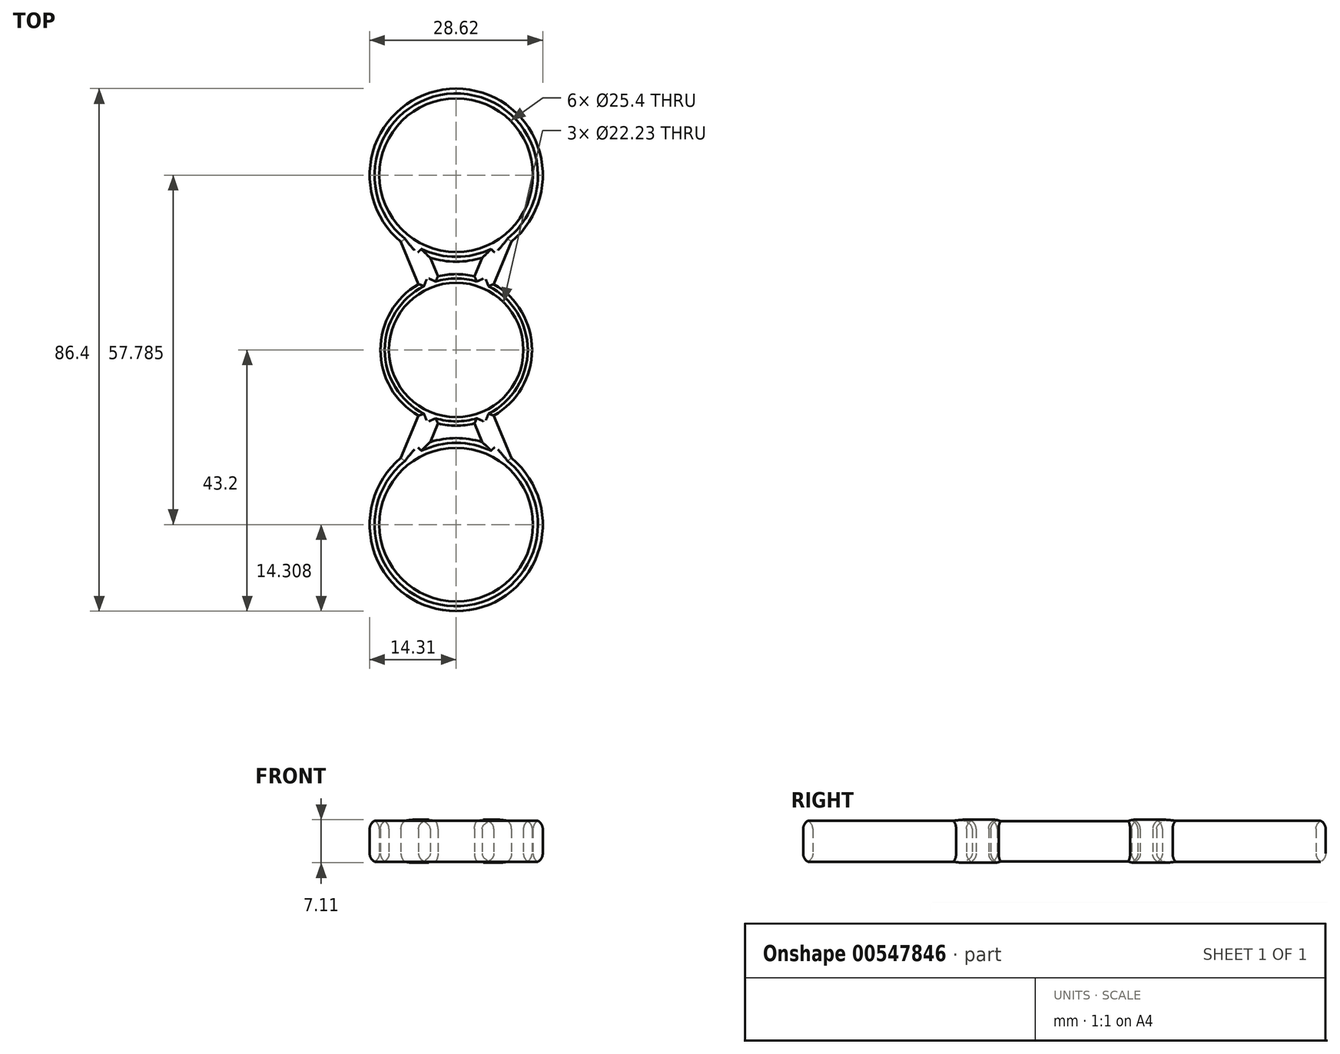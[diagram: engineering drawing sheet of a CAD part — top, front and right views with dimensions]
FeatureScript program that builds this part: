
annotation { "Feature Type Name" : "Feature", "Feature Type Description" : "" }
export const myFeature = defineFeature(function(context is Context, id is Id, definition is map)
    precondition{}
    {
        {
            var Q0;
            Q0=qCreatedBy(makeId("Top.planeOp"),FACE);
            var sketch = newSketch(context, id + "F0", { "sketchPlane" : qUnion([Q0])});
            skCircle(sketch, "E0", {"center": v(0, 0) * mm, "radius": 11.11 * mm});
            skCircle(sketch, "E1", {"center": v(0, 28.9) * mm, "radius": 12.7 * mm});
            skCircle(sketch, "E2", {"center": v(0, -28.9) * mm, "radius": 12.7 * mm});
            skLineSegment(sketch, "E3", {"start": v(-12.07, 24.94) * mm, "end": v(-11.32, 23.13) * mm});
            skLineSegment(sketch, "E4", {"start": v(-4.3, 15.25) * mm, "end": v(-3, 12.16) * mm});
            skLineSegment(sketch, "E5.MirrorCS", {"start": v(4.3, 15.25) * mm, "end": v(3, 12.16) * mm});
            skLineSegment(sketch, "E6.MirrorCS", {"start": v(12.07, 24.94) * mm, "end": v(11.32, 23.13) * mm});
            skLineSegment(sketch, "E7.MirrorCS", {"start": v(-12.07, -24.94) * mm, "end": v(-11.32, -23.13) * mm});
            skLineSegment(sketch, "E8.MirrorCS", {"start": v(-4.3, -15.25) * mm, "end": v(-3, -12.16) * mm});
            skLineSegment(sketch, "E9.MirrorCS", {"start": v(4.3, -15.25) * mm, "end": v(3, -12.16) * mm});
            skLineSegment(sketch, "E10.MirrorCS", {"start": v(12.07, -24.94) * mm, "end": v(11.32, -23.13) * mm});
            skArc(sketch, "E11", {"start": v(-4.3, 15.25) * mm, "mid": v(0, 14.59) * mm, "end": v(4.3, 15.25) * mm});
            skArc(sketch, "E12.MirrorC", {"start": v(-4.3, -15.25) * mm, "mid": v(0, -14.59) * mm, "end": v(4.3, -15.25) * mm});
            skArc(sketch, "E13", {"start": v(-6.23, 10.87) * mm, "mid": v(-12.53, 0) * mm, "end": v(-6.23, -10.87) * mm});
            skPoint(sketch, "E14.orphan", {"position": v(-5.68, 9.55) * mm});
            skPoint(sketch, "E15.orphan", {"position": v(-2.46, 10.84) * mm});
            skArc(sketch, "E16.trimOffspring", {"start": v(3, 12.16) * mm, "mid": v(0, 12.53) * mm, "end": v(-3, 12.16) * mm});
            skPoint(sketch, "E17.orphan", {"position": v(2.46, 10.84) * mm});
            skPoint(sketch, "E18.orphan", {"position": v(5.68, 9.55) * mm});
            skLineSegment(sketch, "E19.trimOffspring", {"start": v(-9.14, 17.89) * mm, "end": v(-6.23, 10.87) * mm});
            skPoint(sketch, "E20.orphan", {"position": v(-5.13, 17.28) * mm});
            skPoint(sketch, "E21.orphan", {"position": v(5.13, 17.28) * mm});
            skLineSegment(sketch, "E22.trimOffspring", {"start": v(9.14, 17.89) * mm, "end": v(6.23, 10.87) * mm});
            skArc(sketch, "E23.trimOffspring", {"start": v(9.14, 17.89) * mm, "mid": v(0, 43.2) * mm, "end": v(-9.14, 17.89) * mm});
            skArc(sketch, "E24.trimOffspring", {"start": v(-3, -12.16) * mm, "mid": v(0, -12.53) * mm, "end": v(3, -12.16) * mm});
            skPoint(sketch, "E25.orphan", {"position": v(-5.68, -9.55) * mm});
            skPoint(sketch, "E26.orphan", {"position": v(-2.46, -10.84) * mm});
            skLineSegment(sketch, "E27.trimOffspring", {"start": v(-9.14, -17.89) * mm, "end": v(-6.23, -10.87) * mm});
            skPoint(sketch, "E28.orphan", {"position": v(-5.13, -17.28) * mm});
            skPoint(sketch, "E29.orphan", {"position": v(2.46, -10.84) * mm});
            skPoint(sketch, "E30.orphan", {"position": v(5.13, -17.28) * mm});
            skArc(sketch, "E31.trimOffspring", {"start": v(9.14, -17.89) * mm, "mid": v(0, -43.2) * mm, "end": v(-9.14, -17.89) * mm});
            skArc(sketch, "E32.trimOffspring", {"start": v(6.23, -10.87) * mm, "mid": v(12.53, 0) * mm, "end": v(6.23, 10.87) * mm});
            skPoint(sketch, "E33.orphan", {"position": v(5.68, -9.55) * mm});
            skLineSegment(sketch, "E34.trimOffspring", {"start": v(9.14, -17.89) * mm, "end": v(6.23, -10.87) * mm});
            skPoint(sketch, "E35.orphan", {"position": v(-32.38, 0) * mm});
            skSolve(sketch);
        }
        {
            var Q0;
            Q0=makeQuery(id+"F0.imprint","IMPRINT",FACE,{"disambiguationData":[TD([[makeQuery(id+"F0.imprint","IMPRINT",EDGE,{"derivedFrom":sQuery(id+"F0.wireOp",EDGE,"E0")}),-1.0]])]});
            extrude(context, id + "F1", {"entities" : qUnion([Q0]), "depth" : 7.11 * mm, "offsetDistance" : 25.4 * mm});
        }
        {
            var Q0;
            Q0=makeQuery(id+"F1.opExtrude","CAP_FACE",FACE,{"disambiguationData":[OSD([sQuery(id+"F0.wireOp",EDGE,"E0"),sQuery(id+"F0.wireOp",EDGE,"E1"),sQuery(id+"F0.wireOp",EDGE,"E2"),sQuery(id+"F0.wireOp",EDGE,"E4"),sQuery(id+"F0.wireOp",EDGE,"E5.MirrorCS"),sQuery(id+"F0.wireOp",EDGE,"E8.MirrorCS"),sQuery(id+"F0.wireOp",EDGE,"E9.MirrorCS"),sQuery(id+"F0.wireOp",EDGE,"E11"),sQuery(id+"F0.wireOp",EDGE,"E12.MirrorC"),sQuery(id+"F0.wireOp",EDGE,"E13"),sQuery(id+"F0.wireOp",EDGE,"E16.trimOffspring"),sQuery(id+"F0.wireOp",EDGE,"E19.trimOffspring"),sQuery(id+"F0.wireOp",EDGE,"E22.trimOffspring"),sQuery(id+"F0.wireOp",EDGE,"E23.trimOffspring"),sQuery(id+"F0.wireOp",EDGE,"E24.trimOffspring"),sQuery(id+"F0.wireOp",EDGE,"E27.trimOffspring"),sQuery(id+"F0.wireOp",EDGE,"E31.trimOffspring"),sQuery(id+"F0.wireOp",EDGE,"E32.trimOffspring"),sQuery(id+"F0.wireOp",EDGE,"E34.trimOffspring")])],"isStart":false});
            var Q1;
            Q1=makeQuery(id+"F1.opExtrude","CAP_FACE",FACE,{"disambiguationData":[OSD([sQuery(id+"F0.wireOp",EDGE,"E0"),sQuery(id+"F0.wireOp",EDGE,"E1"),sQuery(id+"F0.wireOp",EDGE,"E2"),sQuery(id+"F0.wireOp",EDGE,"E4"),sQuery(id+"F0.wireOp",EDGE,"E5.MirrorCS"),sQuery(id+"F0.wireOp",EDGE,"E8.MirrorCS"),sQuery(id+"F0.wireOp",EDGE,"E9.MirrorCS"),sQuery(id+"F0.wireOp",EDGE,"E11"),sQuery(id+"F0.wireOp",EDGE,"E12.MirrorC"),sQuery(id+"F0.wireOp",EDGE,"E13"),sQuery(id+"F0.wireOp",EDGE,"E16.trimOffspring"),sQuery(id+"F0.wireOp",EDGE,"E19.trimOffspring"),sQuery(id+"F0.wireOp",EDGE,"E22.trimOffspring"),sQuery(id+"F0.wireOp",EDGE,"E23.trimOffspring"),sQuery(id+"F0.wireOp",EDGE,"E24.trimOffspring"),sQuery(id+"F0.wireOp",EDGE,"E27.trimOffspring"),sQuery(id+"F0.wireOp",EDGE,"E31.trimOffspring"),sQuery(id+"F0.wireOp",EDGE,"E32.trimOffspring"),sQuery(id+"F0.wireOp",EDGE,"E34.trimOffspring")])],"isStart":true});
            fillet(context, id + "F2", {"entities" : qUnion([Q0, Q1]), "radius" : 1.52 * mm, "tangentPropagation" : true, "allowEdgeOverflow" : false});
        }
    });
